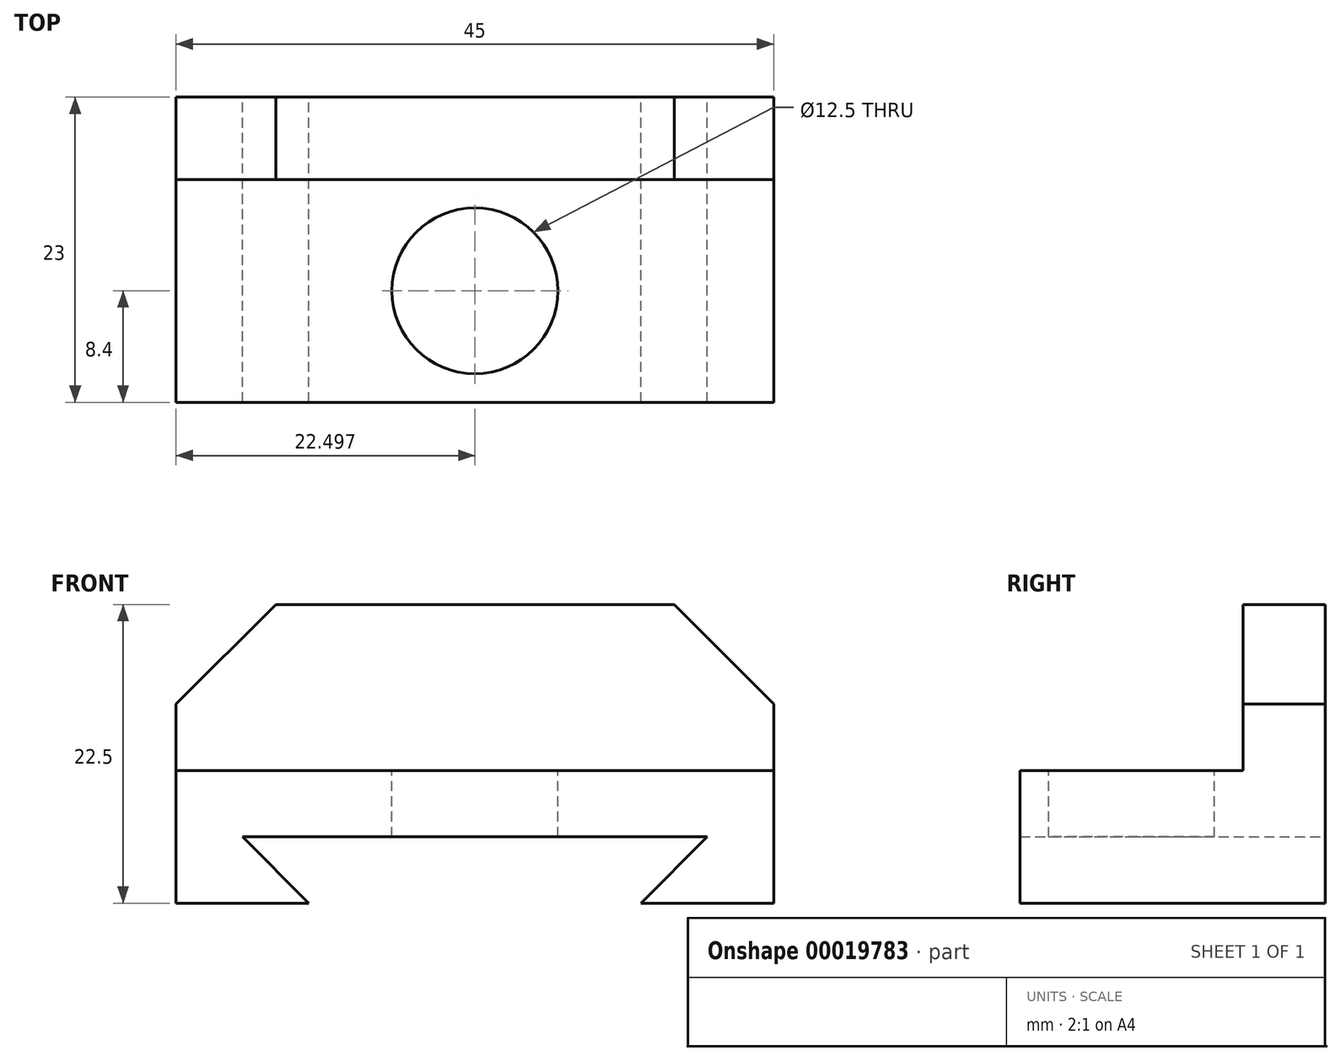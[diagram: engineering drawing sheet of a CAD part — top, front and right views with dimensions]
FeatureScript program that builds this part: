
annotation { "Feature Type Name" : "Feature", "Feature Type Description" : "" }
export const myFeature = defineFeature(function(context is Context, id is Id, definition is map)
    precondition{}
    {
        {
            var Q0;
            Q0=qCreatedBy(makeId("Front.planeOp"),FACE);
            var sketch = newSketch(context, id + "F0", { "sketchPlane" : qUnion([Q0])});
            skLineSegment(sketch, "E0", {"start": v(-7.22, -5) * mm, "end": v(-17.22, -5) * mm});
            skLineSegment(sketch, "E1", {"start": v(-17.22, -5) * mm, "end": v(-17.22, 5) * mm});
            skLineSegment(sketch, "E2", {"start": v(-17.22, 5) * mm, "end": v(27.78, 5) * mm});
            skLineSegment(sketch, "E3", {"start": v(27.78, 5) * mm, "end": v(27.78, -5) * mm});
            skLineSegment(sketch, "E4", {"start": v(27.78, -5) * mm, "end": v(17.78, -5) * mm});
            skLineSegment(sketch, "E5", {"start": v(-7.22, -5) * mm, "end": v(-12.22, 0) * mm});
            skLineSegment(sketch, "E6", {"start": v(-12.22, 0) * mm, "end": v(22.78, 0) * mm});
            skLineSegment(sketch, "E7", {"start": v(22.78, 0) * mm, "end": v(17.78, -5) * mm});
            skSolve(sketch);
        }
        {
            var Q0;
            Q0 = qSketchRegion(id + "F0", true);
            extrude(context, id + "F1", {"entities" : qUnion([Q0]), "depth" : 23 * mm});
        }
        {
            var Q0;
            Q0=makeQuery(id+"F1.opExtrude","SWEPT_FACE",FACE,{"disambiguationData":[OSD([sQuery(id+"F0.wireOp",EDGE,"E2")])]});
            var sketch = newSketch(context, id + "F2", { "sketchPlane" : qUnion([Q0])});
            skLineSegment(sketch, "E8", {"start": v(-17.22, 0) * mm, "end": v(-17.22, -6.2) * mm});
            skLineSegment(sketch, "E9", {"start": v(-17.22, -6.2) * mm, "end": v(27.78, -6.2) * mm});
            skLineSegment(sketch, "E10", {"start": v(27.78, -6.2) * mm, "end": v(27.78, 0) * mm});
            skLineSegment(sketch, "E11", {"start": v(27.78, 0) * mm, "end": v(-17.22, 0) * mm});
            skCircle(sketch, "E12", {"center": v(5.28, -14.6) * mm, "radius": 6.25 * mm});
            skSolve(sketch);
        }
        {
            var Q0;
            Q0=makeQuery(id+"F2.imprint","IMPRINT",FACE,{"disambiguationData":[TD([[makeQuery(id+"F2.imprint","IMPRINT",EDGE,{"derivedFrom":sQuery(id+"F2.wireOp",EDGE,"E12")}),1.0]])]});
            extrude(context, id + "F3", {"entities" : qUnion([Q0]), "operationType" : NewBodyOperationType.REMOVE, "oppositeDirection" : true, "depth" : 25 * mm});
        }
        {
            var Q0;
            Q0=makeQuery(id+"F1.opExtrude","SWEPT_FACE",FACE,{"disambiguationData":[OSD([sQuery(id+"F0.wireOp",EDGE,"E2")])]});
            var sketch = newSketch(context, id + "F4", { "sketchPlane" : qUnion([Q0])});
            skLineSegment(sketch, "E13", {"start": v(-17.22, -6.2) * mm, "end": v(27.78, -6.2) * mm});
            skLineSegment(sketch, "E14", {"start": v(27.78, -6.2) * mm, "end": v(27.78, 0) * mm});
            skLineSegment(sketch, "E15", {"start": v(27.78, 0) * mm, "end": v(-17.22, 0) * mm});
            skLineSegment(sketch, "E16", {"start": v(-17.22, 0) * mm, "end": v(-17.22, -6.2) * mm});
            skSolve(sketch);
        }
        {
            var Q0;
            Q0=makeQuery(id+"F4.imprint","IMPRINT",FACE,{"disambiguationData":[TD([[makeQuery(id+"F4.imprint","IMPRINT",EDGE,{"derivedFrom":sQuery(id+"F4.wireOp",EDGE,"E13")}),1.0]])]});
            extrude(context, id + "F5", {"entities" : qUnion([Q0]), "operationType" : NewBodyOperationType.ADD, "depth" : 12.5 * mm});
        }
        {
            var Q0;
            Q0=makeQuery(id+"F5.opExtrude","SWEPT_FACE",FACE,{"disambiguationData":[OSD([sQuery(id+"F4.wireOp",EDGE,"E13")])]});
            var sketch = newSketch(context, id + "F6", { "sketchPlane" : qUnion([Q0])});
            skLineSegment(sketch, "E17", {"start": v(27.78, 5) * mm, "end": v(27.78, 10) * mm});
            skLineSegment(sketch, "E18", {"start": v(-17.22, 10) * mm, "end": v(-17.22, 5) * mm});
            skLineSegment(sketch, "E19", {"start": v(5.28, 17.5) * mm, "end": v(-9.72, 17.5) * mm});
            skLineSegment(sketch, "E20", {"start": v(-9.72, 17.5) * mm, "end": v(-17.22, 10) * mm});
            skLineSegment(sketch, "E21", {"start": v(5.28, 17.5) * mm, "end": v(20.28, 17.5) * mm});
            skLineSegment(sketch, "E22", {"start": v(20.28, 17.5) * mm, "end": v(27.78, 10) * mm});
            skSolve(sketch);
        }
        {
            var Q0;
            {var subQ2=sQuery(id+"F6.wireOp",EDGE,"E20");Q0=makeQuery(id+"F6.imprint","IMPRINT",FACE,{"disambiguationData":[TD([[makeQuery(id+"F6.imprint","IMPRINT",EDGE,{"derivedFrom":subQ2}),-1.0]])]});}
            var Q1;
            {var subQ2=sQuery(id+"F6.wireOp",EDGE,"E22");Q1=makeQuery(id+"F6.imprint","IMPRINT",FACE,{"disambiguationData":[TD([[makeQuery(id+"F6.imprint","IMPRINT",EDGE,{"derivedFrom":subQ2}),1.0]])]});}
            extrude(context, id + "F7", {"entities" : qUnion([Q0, Q1]), "operationType" : NewBodyOperationType.REMOVE, "oppositeDirection" : true, "depth" : 25 * mm});
        }
    });
